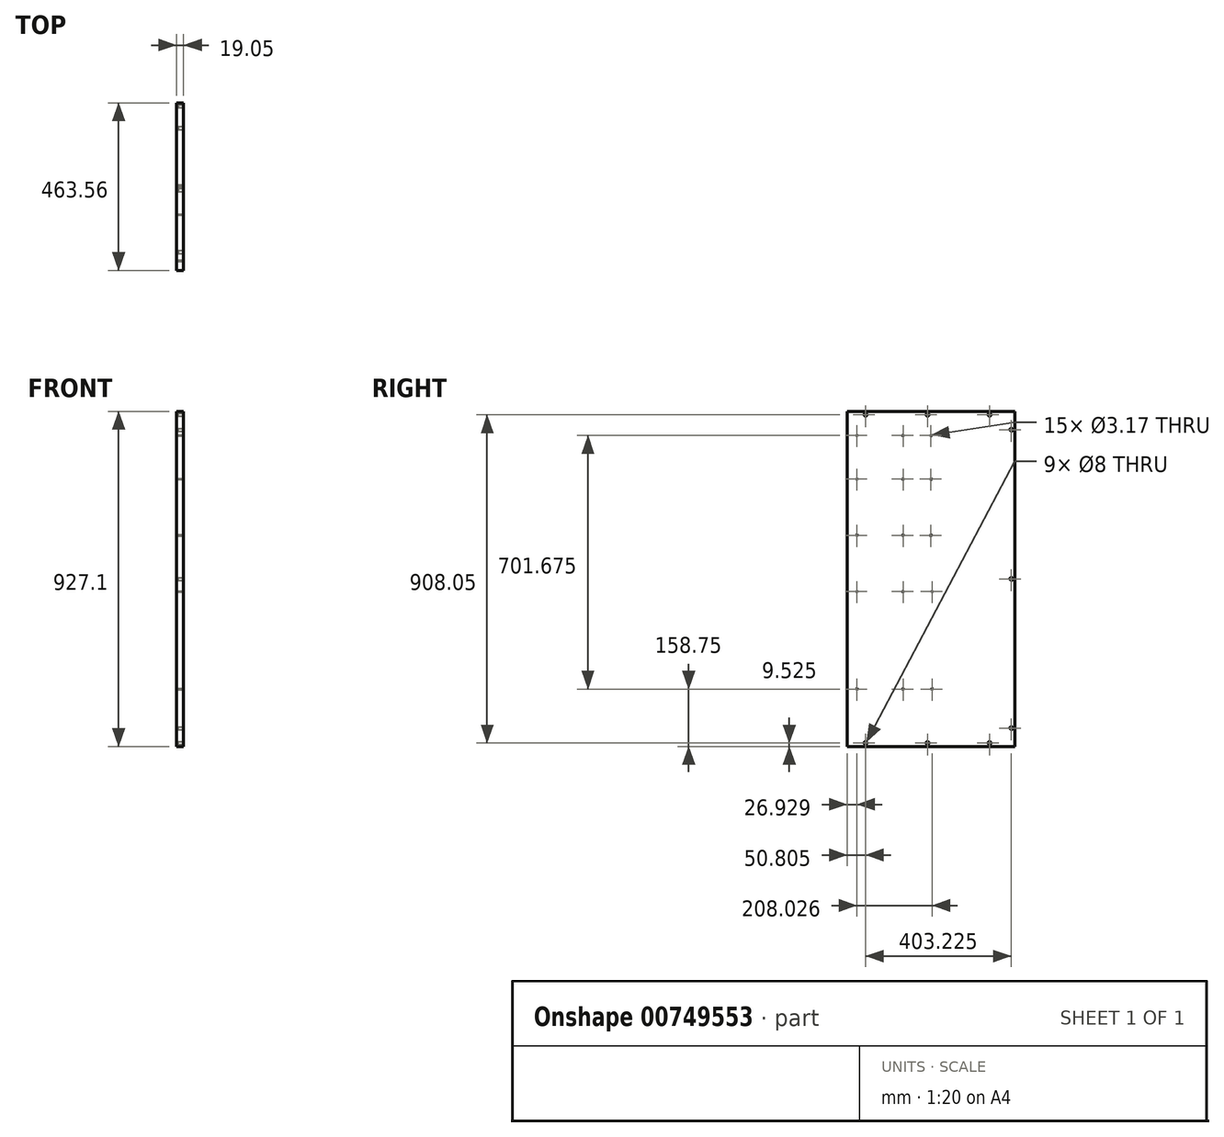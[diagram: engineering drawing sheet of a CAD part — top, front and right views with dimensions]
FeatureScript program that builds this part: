
annotation { "Feature Type Name" : "Feature", "Feature Type Description" : "" }
export const myFeature = defineFeature(function(context is Context, id is Id, definition is map)
    precondition{}
    {
        {
            var Q0;
            Q0=qCreatedBy(makeId("Right.planeOp"),FACE);
            var sketch = newSketch(context, id + "F0", { "sketchPlane" : qUnion([Q0])});
            skLineSegment(sketch, "E0.bottom", {"start": v(231.77, 463.55) * mm, "end": v(-231.78, 463.55) * mm});
            skLineSegment(sketch, "E0.top", {"start": v(231.77, -463.55) * mm, "end": v(-231.78, -463.55) * mm});
            skLineSegment(sketch, "E0.left", {"start": v(231.77, 463.55) * mm, "end": v(231.77, -463.55) * mm});
            skLineSegment(sketch, "E0.right", {"start": v(-231.78, 463.55) * mm, "end": v(-231.78, -463.55) * mm});
            skPoint(sketch, "E0.middle", {"position": v(0, 0) * mm});
            skSolve(sketch);
        }
        {
            var Q0;
            Q0=makeQuery(id+"F0.imprint","IMPRINT",FACE,{"disambiguationData":[TD([[makeQuery(id+"F0.imprint","IMPRINT",EDGE,{"derivedFrom":sQuery(id+"F0.wireOp",EDGE,"E0.bottom")}),1.0]])]});
            extrude(context, id + "F1", {"entities" : qUnion([Q0]), "depth" : 19.05 * mm, "offsetDistance" : 25.4 * mm});
        }
        {
            var Q0;
            Q0=makeQuery(id+"F1.opExtrude","CAP_FACE",FACE,{"disambiguationData":[OSD([sQuery(id+"F0.wireOp",EDGE,"E0.bottom"),sQuery(id+"F0.wireOp",EDGE,"E0.top"),sQuery(id+"F0.wireOp",EDGE,"E0.left"),sQuery(id+"F0.wireOp",EDGE,"E0.right")])],"isStart":false});
            var sketch = newSketch(context, id + "F2", { "sketchPlane" : qUnion([Q0])});
            skLineSegment(sketch, "E1", {"start": v(-231.78, 463.55) * mm, "end": v(-231.78, 454.03) * mm});
            skLineSegment(sketch, "E2", {"start": v(-231.78, 454.03) * mm, "end": v(-180.98, 454.03) * mm});
            skLineSegment(sketch, "E3", {"start": v(231.77, 463.55) * mm, "end": v(231.77, 454.02) * mm});
            skLineSegment(sketch, "E4", {"start": v(231.77, 454.02) * mm, "end": v(161.92, 454.02) * mm});
            skLineSegment(sketch, "E5", {"start": v(-231.78, 454.03) * mm, "end": v(-9.53, 454.03) * mm});
            skLineSegment(sketch, "E6", {"start": v(-231.78, -463.55) * mm, "end": v(-231.78, -454.02) * mm});
            skLineSegment(sketch, "E7", {"start": v(-231.78, -454.02) * mm, "end": v(-180.98, -454.02) * mm});
            skLineSegment(sketch, "E8", {"start": v(-231.78, -454.02) * mm, "end": v(-9.53, -454.02) * mm});
            skLineSegment(sketch, "E9", {"start": v(231.77, -463.55) * mm, "end": v(231.77, -454.02) * mm});
            skLineSegment(sketch, "E10", {"start": v(231.77, -454.02) * mm, "end": v(161.92, -454.02) * mm});
            skPoint(sketch, "E11", {"position": v(-180.98, 454.03) * mm});
            skPoint(sketch, "E12", {"position": v(-9.53, 454.03) * mm});
            skPoint(sketch, "E13", {"position": v(161.92, 454.02) * mm});
            skPoint(sketch, "E14", {"position": v(-180.98, -454.02) * mm});
            skPoint(sketch, "E15", {"position": v(-9.53, -454.02) * mm});
            skPoint(sketch, "E16", {"position": v(161.92, -454.02) * mm});
            skLineSegment(sketch, "E17", {"start": v(231.77, 463.55) * mm, "end": v(222.25, 463.55) * mm});
            skLineSegment(sketch, "E18", {"start": v(222.25, 463.55) * mm, "end": v(222.25, 412.75) * mm});
            skLineSegment(sketch, "E19", {"start": v(231.77, -463.55) * mm, "end": v(222.25, -463.55) * mm});
            skLineSegment(sketch, "E20", {"start": v(222.25, -463.55) * mm, "end": v(222.25, -412.75) * mm});
            skLineSegment(sketch, "E21", {"start": v(231.77, 0) * mm, "end": v(222.25, 0) * mm});
            skPoint(sketch, "E22", {"position": v(222.25, 412.75) * mm});
            skPoint(sketch, "E23", {"position": v(222.25, 0) * mm});
            skPoint(sketch, "E24", {"position": v(222.25, -412.75) * mm});
            skSolve(sketch);
        }
        {
            var Q0;
            Q0=sQuery(id+"F2.wireOp",VERTEX,"E11");
            var Q1;
            Q1=sQuery(id+"F2.wireOp",VERTEX,"E12");
            var Q2;
            Q2=sQuery(id+"F2.wireOp",VERTEX,"E13");
            var Q3;
            Q3=sQuery(id+"F2.wireOp",VERTEX,"E22");
            var Q4;
            Q4=sQuery(id+"F2.wireOp",VERTEX,"E23");
            var Q5;
            Q5=sQuery(id+"F2.wireOp",VERTEX,"E24");
            var Q6;
            Q6=sQuery(id+"F2.wireOp",VERTEX,"E16");
            var Q7;
            Q7=sQuery(id+"F2.wireOp",VERTEX,"E15");
            var Q8;
            Q8=sQuery(id+"F2.wireOp",VERTEX,"E14");
            var Q9;
            Q9=makeQuery(id+"F1.opExtrude","SWEPT_BODY",BODY,{"disambiguationData":[OSD([sQuery(id+"F0.wireOp",EDGE,"E0.bottom"),sQuery(id+"F0.wireOp",EDGE,"E0.top"),sQuery(id+"F0.wireOp",EDGE,"E0.left"),sQuery(id+"F0.wireOp",EDGE,"E0.right")])]});
            hole(context, id + "F3", {"style" : HoleStyle.SIMPLE, "endStyle" : HoleEndStyle.BLIND, "holeDiameter" : 8 * mm, "majorDiameter" : 6.35 * mm, "holeDepth" : 14.22 * mm, "isTappedThrough" : true, "tappedDepth" : 12.7 * mm, "tapClearance" : 3, "startFromSketch" : true, "locations" : qUnion([Q0, Q1, Q2, Q3, Q4, Q5, Q6, Q7, Q8]), "scope" : qUnion([Q9])});
        }
        {
            var Q0;
            Q0=makeQuery(id+"F1.opExtrude","CAP_FACE",FACE,{"disambiguationData":[OSD([sQuery(id+"F0.wireOp",EDGE,"E0.bottom"),sQuery(id+"F0.wireOp",EDGE,"E0.top"),sQuery(id+"F0.wireOp",EDGE,"E0.left"),sQuery(id+"F0.wireOp",EDGE,"E0.right")])],"isStart":false});
            var sketch = newSketch(context, id + "F4", { "sketchPlane" : qUnion([Q0])});
            skLineSegment(sketch, "E25", {"start": v(-231.78, -463.55) * mm, "end": v(-231.78, -304.8) * mm});
            skLineSegment(sketch, "E26", {"start": v(-231.78, -304.8) * mm, "end": v(-204.85, -304.8) * mm});
            skLineSegment(sketch, "E27", {"start": v(-231.78, -304.8) * mm, "end": v(-77.09, -304.8) * mm});
            skLineSegment(sketch, "E28", {"start": v(-231.78, -304.8) * mm, "end": v(3.17, -304.8) * mm});
            skPoint(sketch, "E29", {"position": v(-204.85, -304.8) * mm});
            skPoint(sketch, "E30", {"position": v(-77.09, -304.8) * mm});
            skPoint(sketch, "E31", {"position": v(3.17, -304.8) * mm});
            skLineSegment(sketch, "E32", {"start": v(-231.78, -463.55) * mm, "end": v(-231.78, -34.92) * mm});
            skLineSegment(sketch, "E33", {"start": v(-231.78, -34.92) * mm, "end": v(-204.85, -34.92) * mm});
            skLineSegment(sketch, "E34", {"start": v(-231.78, -34.92) * mm, "end": v(-77.09, -34.92) * mm});
            skLineSegment(sketch, "E35", {"start": v(-231.78, -34.92) * mm, "end": v(3.17, -34.92) * mm});
            skPoint(sketch, "E36", {"position": v(-204.85, -34.92) * mm});
            skPoint(sketch, "E37", {"position": v(-77.09, -34.92) * mm});
            skPoint(sketch, "E38", {"position": v(3.17, -34.92) * mm});
            skLineSegment(sketch, "E39", {"start": v(-231.78, -463.55) * mm, "end": v(-231.78, 120.65) * mm});
            skLineSegment(sketch, "E40", {"start": v(-231.78, 120.65) * mm, "end": v(-204.85, 120.65) * mm});
            skLineSegment(sketch, "E41", {"start": v(-204.85, 120.65) * mm, "end": v(-77.09, 120.65) * mm});
            skLineSegment(sketch, "E42", {"start": v(-77.09, 120.65) * mm, "end": v(0, 120.65) * mm});
            skPoint(sketch, "E43", {"position": v(-204.85, 120.65) * mm});
            skPoint(sketch, "E44", {"position": v(-77.09, 120.65) * mm});
            skPoint(sketch, "E45", {"position": v(0, 120.65) * mm});
            skLineSegment(sketch, "E46", {"start": v(-231.78, -463.55) * mm, "end": v(-231.78, 276.23) * mm});
            skLineSegment(sketch, "E47", {"start": v(-231.78, 276.23) * mm, "end": v(-204.85, 276.23) * mm});
            skLineSegment(sketch, "E48", {"start": v(-204.85, 276.23) * mm, "end": v(-77.09, 276.23) * mm});
            skLineSegment(sketch, "E49", {"start": v(-77.09, 276.23) * mm, "end": v(0, 276.23) * mm});
            skPoint(sketch, "E50", {"position": v(-204.85, 276.23) * mm});
            skPoint(sketch, "E51", {"position": v(-77.09, 276.23) * mm});
            skPoint(sketch, "E52", {"position": v(0, 276.23) * mm});
            skLineSegment(sketch, "E53", {"start": v(-231.78, -463.55) * mm, "end": v(-231.78, 396.88) * mm});
            skLineSegment(sketch, "E54", {"start": v(-231.78, 396.88) * mm, "end": v(-204.85, 396.88) * mm});
            skLineSegment(sketch, "E55", {"start": v(-204.85, 396.88) * mm, "end": v(-77.09, 396.88) * mm});
            skLineSegment(sketch, "E56", {"start": v(-77.09, 396.88) * mm, "end": v(0, 396.88) * mm});
            skPoint(sketch, "E57", {"position": v(-204.85, 396.88) * mm});
            skPoint(sketch, "E58", {"position": v(-77.09, 396.88) * mm});
            skPoint(sketch, "E59", {"position": v(0, 396.88) * mm});
            skSolve(sketch);
        }
        {
            var Q0;
            Q0=sQuery(id+"F4.wireOp",VERTEX,"E57");
            var Q1;
            Q1=sQuery(id+"F4.wireOp",VERTEX,"E58");
            var Q2;
            Q2=sQuery(id+"F4.wireOp",VERTEX,"E59");
            var Q3;
            Q3=sQuery(id+"F4.wireOp",VERTEX,"E50");
            var Q4;
            Q4=sQuery(id+"F4.wireOp",VERTEX,"E51");
            var Q5;
            Q5=sQuery(id+"F4.wireOp",VERTEX,"E52");
            var Q6;
            Q6=sQuery(id+"F4.wireOp",VERTEX,"E43");
            var Q7;
            Q7=sQuery(id+"F4.wireOp",VERTEX,"E44");
            var Q8;
            Q8=sQuery(id+"F4.wireOp",VERTEX,"E45");
            var Q9;
            Q9=sQuery(id+"F4.wireOp",VERTEX,"E36");
            var Q10;
            Q10=sQuery(id+"F4.wireOp",VERTEX,"E37");
            var Q11;
            Q11=sQuery(id+"F4.wireOp",VERTEX,"E38");
            var Q12;
            Q12=sQuery(id+"F4.wireOp",VERTEX,"E29");
            var Q13;
            Q13=sQuery(id+"F4.wireOp",VERTEX,"E30");
            var Q14;
            Q14=sQuery(id+"F4.wireOp",VERTEX,"E31");
            var Q15;
            Q15=makeQuery(id+"F1.opExtrude","SWEPT_BODY",BODY,{"disambiguationData":[OSD([sQuery(id+"F0.wireOp",EDGE,"E0.bottom"),sQuery(id+"F0.wireOp",EDGE,"E0.top"),sQuery(id+"F0.wireOp",EDGE,"E0.left"),sQuery(id+"F0.wireOp",EDGE,"E0.right")])]});
            hole(context, id + "F5", {"style" : HoleStyle.SIMPLE, "endStyle" : HoleEndStyle.BLIND, "holeDiameter" : 3.17 * mm, "majorDiameter" : 6.35 * mm, "holeDepth" : 14.22 * mm, "isTappedThrough" : true, "tappedDepth" : 12.7 * mm, "tapClearance" : 3, "startFromSketch" : true, "locations" : qUnion([Q0, Q1, Q2, Q3, Q4, Q5, Q6, Q7, Q8, Q9, Q10, Q11, Q12, Q13, Q14]), "scope" : qUnion([Q15])});
        }
    });
